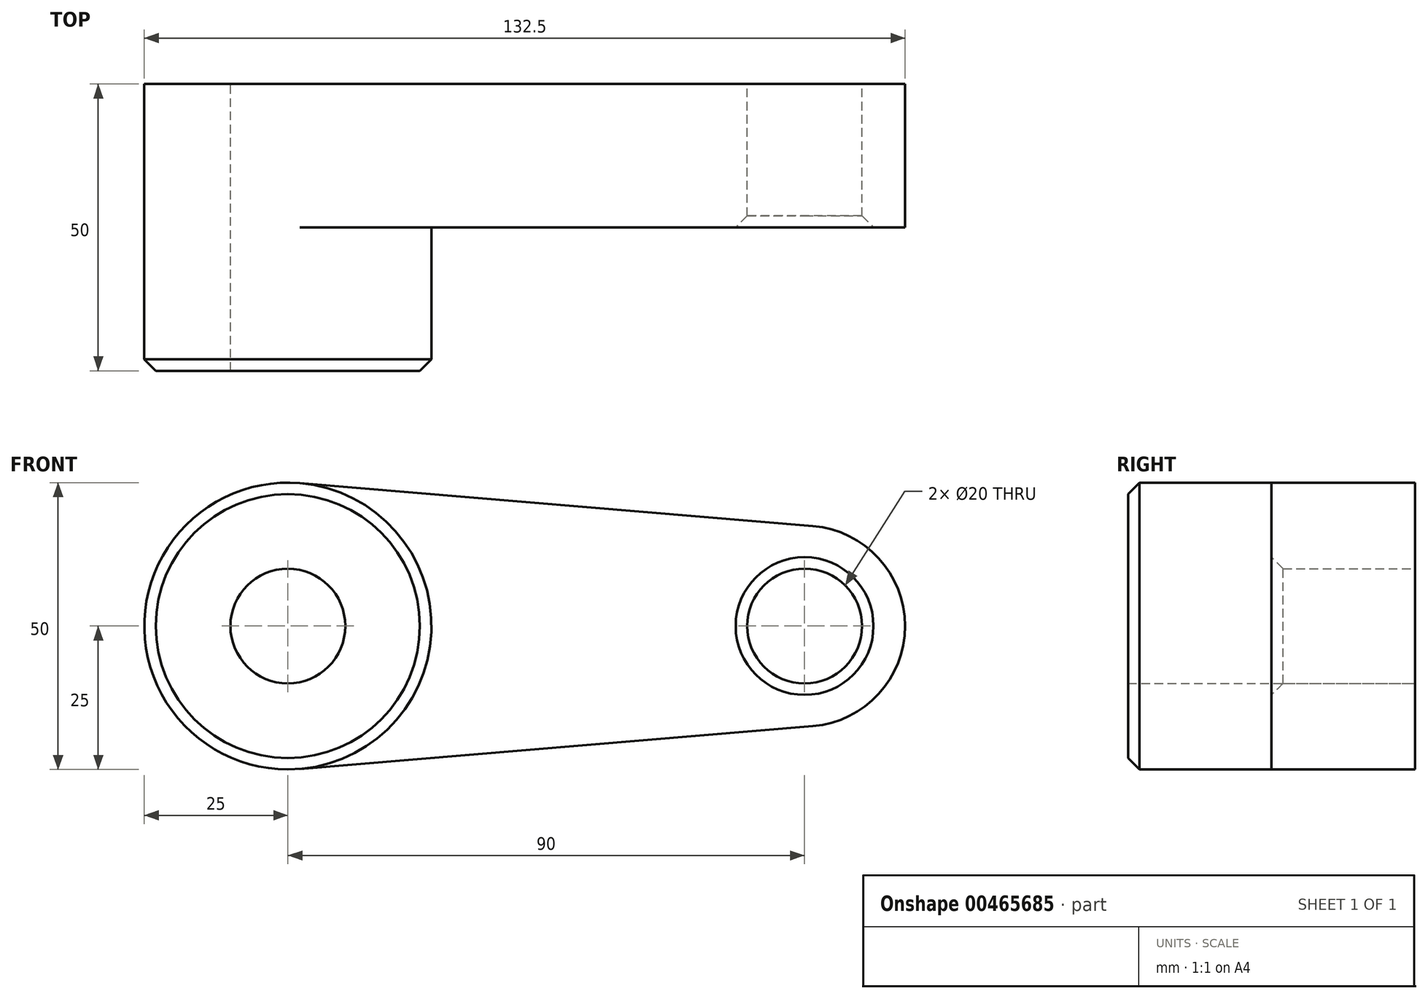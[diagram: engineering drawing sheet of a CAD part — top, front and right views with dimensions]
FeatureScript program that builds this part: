
annotation { "Feature Type Name" : "Feature", "Feature Type Description" : "" }
export const myFeature = defineFeature(function(context is Context, id is Id, definition is map)
    precondition{}
    {
        {
            var Q0;
            Q0=qCreatedBy(makeId("Front.planeOp"),FACE);
            var sketch = newSketch(context, id + "F0", { "sketchPlane" : qUnion([Q0])});
            skCircle(sketch, "E0", {"center": v(0, 0) * mm, "radius": 25 * mm});
            skCircle(sketch, "E1", {"center": v(90, 0) * mm, "radius": 17.5 * mm});
            skLineSegment(sketch, "E2", {"start": v(0, 25.09) * mm, "end": v(91.46, 17.44) * mm});
            skLineSegment(sketch, "E3", {"start": v(2.08, -24.91) * mm, "end": v(91.46, -17.44) * mm});
            skCircle(sketch, "E4", {"center": v(0, 0) * mm, "radius": 10 * mm});
            skCircle(sketch, "E5", {"center": v(90, 0) * mm, "radius": 10 * mm});
            skSolve(sketch);
        }
        {
            var Q0;
            Q0 = qSketchRegion(id + "F0", true);
            extrude(context, id + "F1", {"entities" : qUnion([Q0]), "depth" : 25 * mm});
        }
        {
            var Q0;
            Q0=makeQuery(id+"F0.imprint","IMPRINT",FACE,{"disambiguationData":[TD([[makeQuery(id+"F0.imprint","IMPRINT",EDGE,{"derivedFrom":sQuery(id+"F0.wireOp",EDGE,"E4")}),-1.0]])]});
            extrude(context, id + "F2", {"entities" : qUnion([Q0]), "operationType" : NewBodyOperationType.ADD, "depth" : 50 * mm});
        }
        {
            var Q0;
            Q0=makeQuery(id+"F2.opExtrude","CAP_EDGE",EDGE,{"disambiguationData":[OSD([sQuery(id+"F0.wireOp",EDGE,"E0")])],"isStart":false});
            var Q1;
            Q1=makeQuery(id+"F1.opExtrude","CAP_EDGE",EDGE,{"disambiguationData":[OSD([sQuery(id+"F0.wireOp",EDGE,"E5")])],"isStart":false});
            chamfer(context, id + "F3", {"entities" : qUnion([Q0, Q1]), "width" : 2 * mm, "tangentPropagation" : true});
        }
    });
